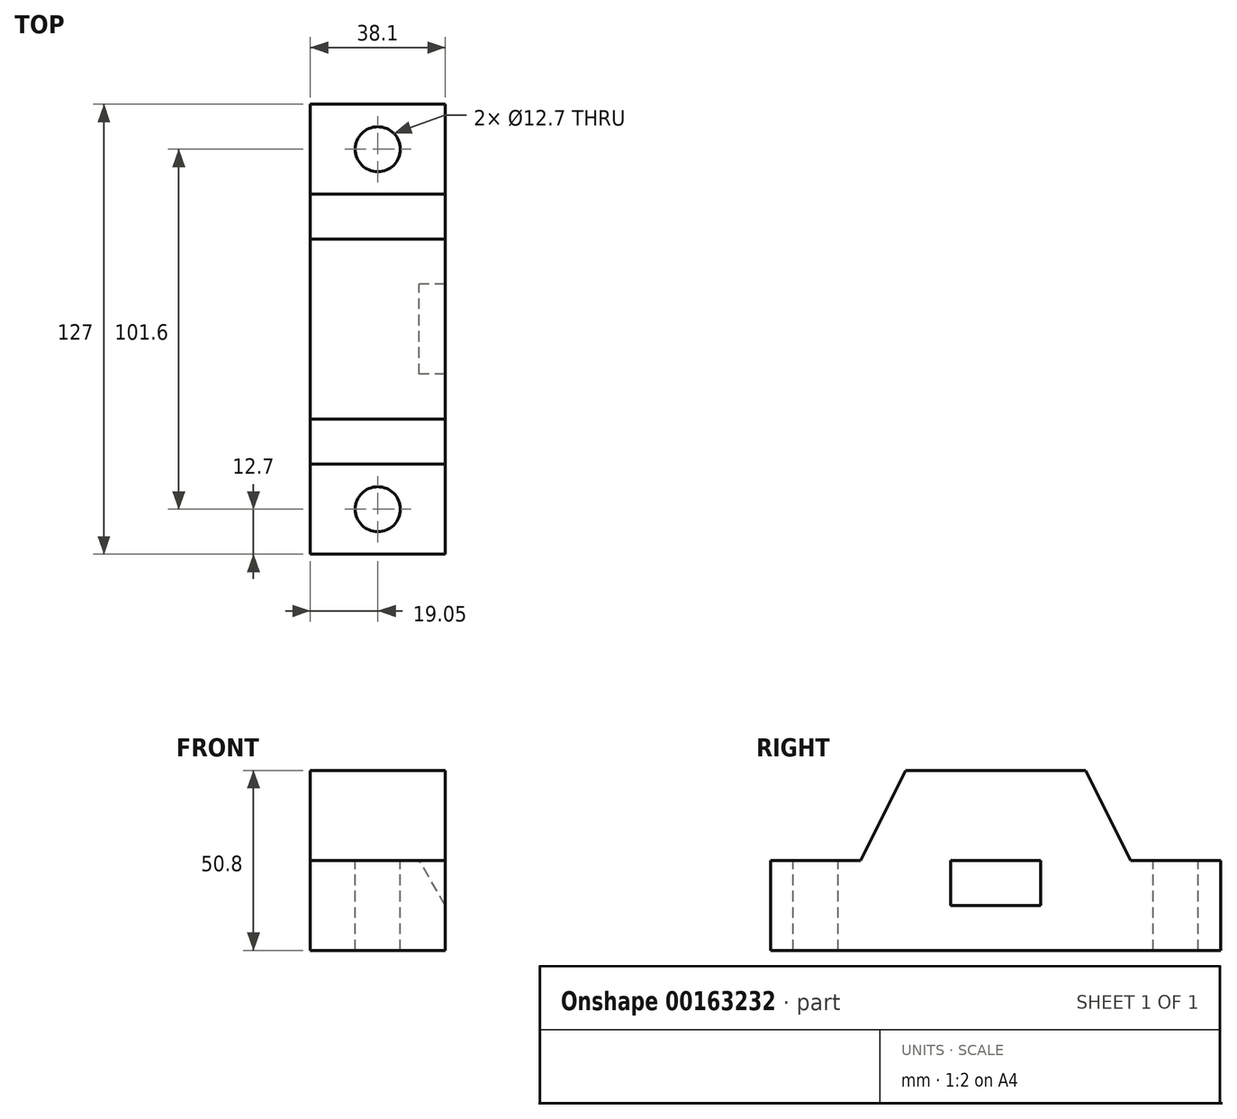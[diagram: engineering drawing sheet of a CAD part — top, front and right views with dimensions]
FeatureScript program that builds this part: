
annotation { "Feature Type Name" : "Feature", "Feature Type Description" : "" }
export const myFeature = defineFeature(function(context is Context, id is Id, definition is map)
    precondition{}
    {
        {
            var Q0;
            Q0=qCreatedBy(makeId("Top.planeOp"),FACE);
            var sketch = newSketch(context, id + "F0", { "sketchPlane" : qUnion([Q0])});
            skLineSegment(sketch, "E0.bottom", {"start": v(19.05, -63.5) * mm, "end": v(-19.05, -63.5) * mm});
            skLineSegment(sketch, "E0.top", {"start": v(19.05, 63.5) * mm, "end": v(-19.05, 63.5) * mm});
            skLineSegment(sketch, "E0.left", {"start": v(19.05, -63.5) * mm, "end": v(19.05, 63.5) * mm});
            skLineSegment(sketch, "E0.right", {"start": v(-19.05, -63.5) * mm, "end": v(-19.05, 63.5) * mm});
            skPoint(sketch, "E0.middle", {"position": v(0, 0) * mm});
            skSolve(sketch);
        }
        {
            var Q0;
            Q0=makeQuery(id+"F0.imprint","IMPRINT",FACE,{"disambiguationData":[TD([[makeQuery(id+"F0.imprint","IMPRINT",EDGE,{"derivedFrom":sQuery(id+"F0.wireOp",EDGE,"E0.bottom")}),-1.0]])]});
            extrude(context, id + "F1", {"entities" : qUnion([Q0]), "depth" : 25.4 * mm});
        }
        {
            var Q0;
            Q0=makeQuery(id+"F1.opExtrude","SWEPT_FACE",FACE,{"disambiguationData":[OSD([sQuery(id+"F0.wireOp",EDGE,"E0.left")])]});
            var sketch = newSketch(context, id + "F2", { "sketchPlane" : qUnion([Q0])});
            skLineSegment(sketch, "E1", {"start": v(-38.1, 25.4) * mm, "end": v(-25.4, 50.8) * mm});
            skLineSegment(sketch, "E2", {"start": v(-25.4, 50.8) * mm, "end": v(25.4, 50.8) * mm});
            skLineSegment(sketch, "E3", {"start": v(25.4, 50.8) * mm, "end": v(38.1, 25.4) * mm});
            skSolve(sketch);
        }
        {
            var Q0;
            {var subQ0=sQuery(id+"F2.wireOp",EDGE,"E1");Q0=makeQuery(id+"F2.imprint","IMPRINT",FACE,{"disambiguationData":[TD([[makeQuery(id+"F2.imprint","IMPRINT",EDGE,{"derivedFrom":subQ0}),-1.0]])]});}
            var Q1;
            Q1=makeQuery(id+"F1.opExtrude","SWEPT_FACE",FACE,{"disambiguationData":[OSD([sQuery(id+"F0.wireOp",EDGE,"E0.right")])]});
            extrude(context, id + "F3", {"entities" : qUnion([Q0]), "operationType" : NewBodyOperationType.ADD, "endBound" : BoundingType.UP_TO_SURFACE, "oppositeDirection" : true, "endBoundEntityFace" : qUnion([Q1]), "depth" : 25.4 * mm});
        }
        {
            var Q0;
            Q0=makeQuery(id+"F1.opExtrude","SWEPT_FACE",FACE,{"disambiguationData":[OSD([sQuery(id+"F0.wireOp",EDGE,"E0.top")])]});
            var sketch = newSketch(context, id + "F4", { "sketchPlane" : qUnion([Q0])});
            skLineSegment(sketch, "E4.0", {"start": v(19.05, 50.8) * mm, "end": v(-19.05, 50.8) * mm});
            skLineSegment(sketch, "E5", {"start": v(-19.05, 12.7) * mm, "end": v(2.95, 50.8) * mm});
            skLineSegment(sketch, "E6", {"start": v(2.95, 50.8) * mm, "end": v(-19.05, 50.8) * mm});
            skLineSegment(sketch, "E7", {"start": v(-19.05, 12.7) * mm, "end": v(-19.05, 50.8) * mm});
            skSolve(sketch);
        }
        {
            var Q0;
            {var subQ0=sQuery(id+"F4.wireOp",EDGE,"E6");Q0=makeQuery(id+"F4.imprint","IMPRINT",FACE,{"disambiguationData":[TD([[makeQuery(id+"F4.imprint","IMPRINT",EDGE,{"derivedFrom":subQ0}),1.0]])]});}
            var Q1;
            {var subQ0=sQuery(id+"F4.wireOp",EDGE,"E7");var subQ2=sQuery(id+"F0.wireOp",EDGE,"E0.top");var subQ4=makeQuery(id+"F1.opExtrude","CAP_EDGE",EDGE,{"disambiguationData":[OSD([subQ2])],"isStart":false});var subQ6=makeQuery(id+"F4.imprint","INTERSECT",VERTEX,{"derivedFrom":[subQ4,subQ0]});Q1=makeQuery(id+"F4.imprint","IMPRINT",FACE,{"disambiguationData":[TD([[makeQuery(id+"F4.imprint","IMPRINT",EDGE,{"disambiguationData":[TD([[subQ6,-1.0]])],"derivedFrom":subQ4}),-1.0]])]});}
            extrude(context, id + "F5", {"entities" : qUnion([Q0, Q1]), "operationType" : NewBodyOperationType.REMOVE, "oppositeDirection" : true, "depth" : 76.2 * mm, "hasSecondDirection" : true, "secondDirectionOppositeDirection" : true, "secondDirectionDepth" : 50.8 * mm});
        }
        {
            var Q0;
            {var subQ1=sQuery(id+"F0.wireOp",EDGE,"E0.left");var subQ2=sQuery(id+"F0.wireOp",EDGE,"E0.right");var subQ3=sQuery(id+"F0.wireOp",EDGE,"E0.bottom");Q0=makeQuery(id+"F3.boolean.opBoolean","SPLIT",FACE,{"disambiguationData":[TD([makeQuery(id+"F1.opExtrude","SWEPT_FACE",FACE,{"disambiguationData":[OSD([subQ3])]})])],"derivedFrom":makeQuery(id+"F1.opExtrude","CAP_FACE",FACE,{"disambiguationData":[OSD([subQ3,sQuery(id+"F0.wireOp",EDGE,"E0.top"),subQ1,subQ2])],"isStart":false})});}
            var sketch = newSketch(context, id + "F6", { "sketchPlane" : qUnion([Q0])});
            skPoint(sketch, "E8", {"position": v(0, -50.8) * mm});
            skPoint(sketch, "E9", {"position": v(0, 50.8) * mm});
            skSolve(sketch);
        }
        {
            var Q0;
            Q0=sQuery(id+"F6.wireOp",VERTEX,"E8");
            var Q1;
            Q1=sQuery(id+"F6.wireOp",VERTEX,"E9");
            var Q2;
            Q2=makeQuery(id+"F1.opExtrude","SWEPT_BODY",BODY,{"disambiguationData":[OSD([sQuery(id+"F0.wireOp",EDGE,"E0.bottom"),sQuery(id+"F0.wireOp",EDGE,"E0.top"),sQuery(id+"F0.wireOp",EDGE,"E0.left"),sQuery(id+"F0.wireOp",EDGE,"E0.right")])]});
            hole(context, id + "F7", {"style" : HoleStyle.SIMPLE, "endStyle" : HoleEndStyle.THROUGH, "holeDiameter" : 12.7 * mm, "locations" : qUnion([Q0, Q1]), "scope" : qUnion([Q2]), "isTappedThrough" : true});
        }
    });
